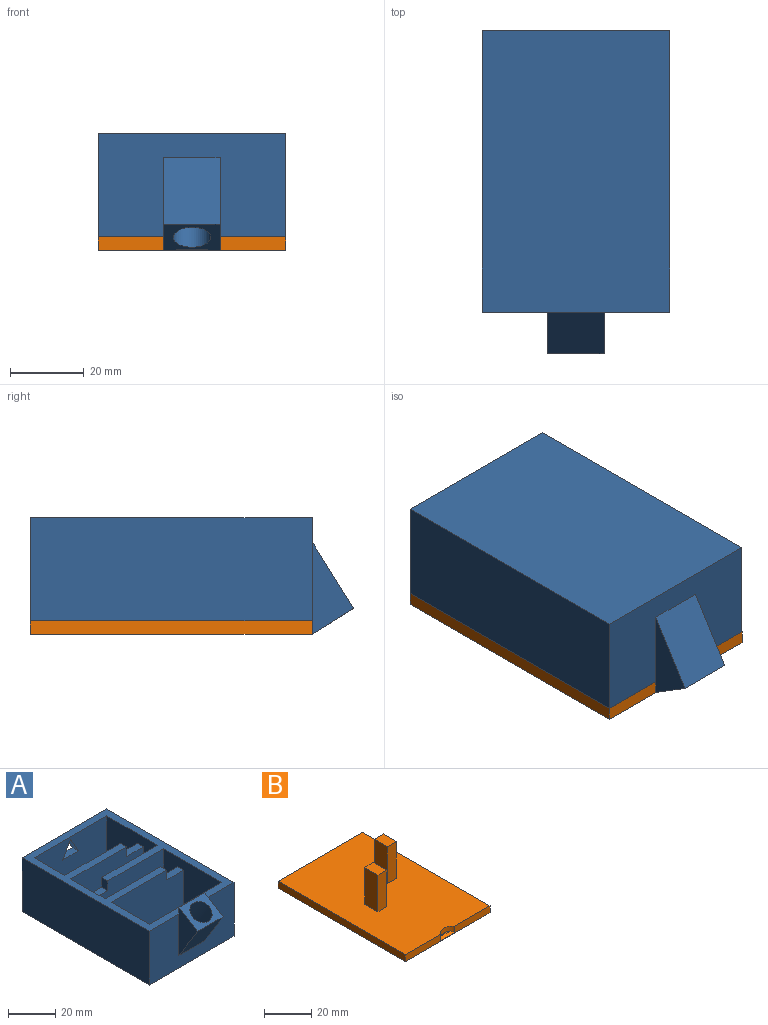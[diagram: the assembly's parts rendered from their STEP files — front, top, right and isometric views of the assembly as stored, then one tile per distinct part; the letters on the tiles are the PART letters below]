
ASSEMBLY  parts=2 mates=1
PART A: 45 faces, bbox 52.1x88.9x36.7 mm
  f0: plane 2.5x0.58mm, normal (0,-1,0), area 0.3mm2, adj f1,f44
  f1: cylinder r=5.08mm len=33.59mm, axis (0,-0.53,0.85), area 929.2mm2, adj f0,f2,f41,f42,f43,f44
  f2: cylinder r=3.76mm len=7.51mm, axis (0,0,-1), area 34mm2, adj f1,f3,f41
  f3: cylinder r=6.35mm len=29.17mm, axis (0,-0.53,0.85), area 479.3mm2, adj f2,f4,f40,f41
  f4: plane 43.52x25.4mm, normal (0,1,0), area 871.3mm2, adj f3,f5,f38,f39,f40
  f5: plane 34.98x25.4mm, normal (-1,0,0), area 814.5mm2, adj f4,f6,f8,f9,f36,f37,f38,f40
  f6: plane 43.52x25.4mm, normal (0,-1,0), area 1053.8mm2, adj f5,f7,f8,f38,f39,f40
  f7: plane 5.08x3.64mm, normal (1,0,0), area 18.5mm2, adj f6,f8,f9,f38
  f8: plane 10.17x3.64mm, normal (0,0,1), area 37mm2, adj f5,f6,f7,f9
  f9: plane 43.52x25.4mm, normal (0,1,0), area 1053.8mm2, adj f5,f7,f8,f10,f36,f38
  f10: plane 25.4x20.52mm, normal (1,0,0), area 447.6mm2, adj f9,f11,f32,f33,f35,f36,f37,f38
  f11: plane 43.52x25.4mm, normal (0,-1,0), area 1053.9mm2, adj f10,f12,f30,f31,f32,f38
  f12: plane 5.08x3.63mm, normal (1,0,0), area 18.5mm2, adj f11,f13,f30,f38
  f13: plane 43.52x25.4mm, normal (0,1,0), area 1053.9mm2, adj f12,f14,f29,f30,f31,f38
  f14: plane 25.4x18.36mm, normal (1,0,0), area 466.3mm2, adj f13,f15,f29,f38
  f15: plane 43.52x25.4mm, normal (0,-1,0), area 1066.8mm2, adj f14,f16,f27,f28,f29,f31,f38
  f16: plane 8.09x4.76mm, normal (-0.86,0,-0.51), area 34.2mm2, adj f15,f17,f27,f28
  f17: plane 50.8x27.94mm, normal (0,1,0), area 1380.7mm2, adj f16,f18,f25,f26,f27,f28,f38
  f18: plane 76.32x50.8mm, normal (0,0,-1), area 3877.2mm2, adj f17,f19,f25,f26
  f19: plane 50.8x27.94mm, normal (0,-1,0), area 1094.8mm2, adj f18,f20,f21,f24,f25,f26,f38
  f20: plane 17.96x15.19mm, normal (0,-0.85,-0.53), area 321.7mm2, adj f19,f21,f24,f43
  f21: plane 24.98x11.23mm, normal (1,0,0), area 140.2mm2, adj f19,f20,f22,f43
  f22: plane 15.19x3.61mm, normal (0,1,0), area 36.6mm2, adj f21,f23,f24,f38,f43
  f23: cylinder r=6.35mm len=8.53mm, axis (0,-0.53,0.85), area 22.6mm2, adj f22,f38
  f24: plane 24.98x11.23mm, normal (-1,0,0), area 140.2mm2, adj f19,f20,f22,f43
  f25: plane 76.32x27.94mm, normal (1,0,0), area 2132.4mm2, adj f17,f18,f19,f38
  f26: plane 76.32x27.94mm, normal (-1,0,0), area 2132.4mm2, adj f17,f18,f19,f38
  f27: plane 8.09x4.78mm, normal (0.86,0,-0.51), area 34.2mm2, adj f15,f16,f17,f28
  f28: plane 9.54x3.64mm, normal (0,0,1), area 34.7mm2, adj f15,f16,f17,f27
  f29: plane 43.52x18.36mm, normal (0,0,1), area 799mm2, adj f13,f14,f15,f31
  f30: plane 10.15x3.63mm, normal (0,0,1), area 36.9mm2, adj f11,f12,f13,f31
  f31: plane 30.44x25.4mm, normal (-1,0,0), area 699.4mm2, adj f11,f13,f15,f29,f30,f32,f33,f38
  f32: plane 43.52x8.45mm, normal (0,0,1), area 367.8mm2, adj f10,f11,f31,f33
  f33: plane 43.52x25.4mm, normal (0,1,0), area 1053.8mm2, adj f10,f31,f32,f34,f35,f38
  f34: plane 5.08x3.62mm, normal (-1,0,0), area 18.4mm2, adj f33,f35,f37,f38
  f35: plane 10.16x3.62mm, normal (0,0,1), area 36.8mm2, adj f10,f33,f34,f37
  f36: plane 43.52x8.45mm, normal (0,0,1), area 367.6mm2, adj f5,f9,f10,f37
  f37: plane 43.52x25.4mm, normal (0,-1,0), area 1053.8mm2, adj f5,f10,f34,f35,f36,f38
  f38: plane 76.32x50.8mm, normal (0,0,1), area 1224.5mm2, adj f4,f5,f6,f7,f9,f10,f11,f12
  f39: plane 25.4x22.89mm, normal (1,0,0), area 581.4mm2, adj f4,f6,f38,f40
  f40: plane 43.52x22.89mm, normal (0,0,1), area 849.9mm2, adj f3,f4,f5,f6,f39
  f41: cylinder r=5.14mm len=7.5mm, axis (0,0,-1), area 27.3mm2, adj f1,f2,f3
  f42: plane 13.31x11.49mm, normal (0,0,1), area 95.5mm2, adj f1
  f43: plane 15.19x11.23mm, normal (0,-0.53,0.85), area 120mm2, adj f1,f20,f21,f22,f24
  f44: plane 2.14x0.1mm, normal (0,0.53,-0.85), area 0.2mm2, adj f0,f1
PART B: 19 faces, bbox 50.8x76.3x22.7 mm
  f0: plane 50.8x3.63mm, normal (0,-1,0), area 155.8mm2, adj f2,f3,f4,f5,f7,f8
  f1: plane 50.8x3.63mm, normal (0,1,0), area 184.5mm2, adj f2,f3,f4,f8
  f2: plane 76.32x3.63mm, normal (1,0,0), area 277.2mm2, adj f0,f1,f4,f8
  f3: plane 76.32x3.63mm, normal (-1,0,0), area 277.2mm2, adj f0,f1,f4,f8
  f4: plane 76.32x50.8mm, normal (0,0,-1), area 3877.2mm2, adj f0,f1,f2,f3
  f5: cylinder r=5.34mm len=8.5mm, axis (0,0,1), area 25mm2, adj f0,f6,f7,f8
  f6: plane 5.74x0.84mm, normal (0,0,1), area 3.3mm2, adj f5,f7
  f7: plane 8.5x1.27mm, normal (0,-0.62,0.78), area 11.8mm2, adj f0,f5,f6
  f8: plane 76.32x50.8mm, normal (0,0,1), area 3778.3mm2, adj f0,f1,f2,f3,f5,f9,f10,f11
  f9: plane 19.05x5.4mm, normal (0,1,0), area 102.8mm2, adj f8,f10,f12,f18
  f10: plane 19.05x8.01mm, normal (1,0,0), area 152.5mm2, adj f8,f9,f11,f18
  f11: plane 19.05x5.4mm, normal (0,-1,0), area 102.8mm2, adj f8,f10,f12,f18
  f12: plane 19.05x8.01mm, normal (-1,0,0), area 152.5mm2, adj f8,f9,f11,f18
  f13: plane 19.05x5.39mm, normal (0,1,0), area 102.8mm2, adj f8,f14,f16,f17
  f14: plane 19.05x8mm, normal (1,0,0), area 152.3mm2, adj f8,f13,f15,f17
  f15: plane 19.05x5.39mm, normal (0,-1,0), area 102.8mm2, adj f8,f14,f16,f17
  f16: plane 19.05x8mm, normal (-1,0,0), area 152.3mm2, adj f8,f13,f15,f17
  f17: plane 8x5.39mm, normal (0,0,1), area 43.1mm2, adj f13,f14,f15,f16
  f18: plane 8.01x5.4mm, normal (0,0,1), area 43.2mm2, adj f9,f10,f11,f12
PLACE A rot(axis=(0,-1,0),180deg) t=(-108.39,0,-43.65)mm
PLACE B t=(-98.01,0,31.46)mm
MATE fastened B.f8 <-> A.f38  axis (0,0,1) through (-184.59,-38.17,-18.25)mm
